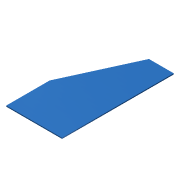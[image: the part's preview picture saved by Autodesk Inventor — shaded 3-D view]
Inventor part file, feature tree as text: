
AUTODESK INVENTOR PART (.ipt)
format: ipt  version: 2014 (Build 180170000, 170)  size: 82,944 bytes
history: native  units: mm
features: extrude x2, sketch x1
ambient origin geometry x8: Origin, YZ Plane, XZ Plane, XY Plane, X Axis, Y Axis, Z Axis, Center Point
bodies: Solid1 (feature_tree)
feature tree (3):
  extrude  "Extrusion1"  Depth=450.0mm
  extrude  "Extrusion2"  Depth=4.0mm TaperAngle=0.0deg
  sketch  "Sketch1"  dims[d0=225.0mm d1=450.0mm d2=4.0mm d3=0.0mm d4=4.0mm d5=0.0mm d8=175.0mm]
